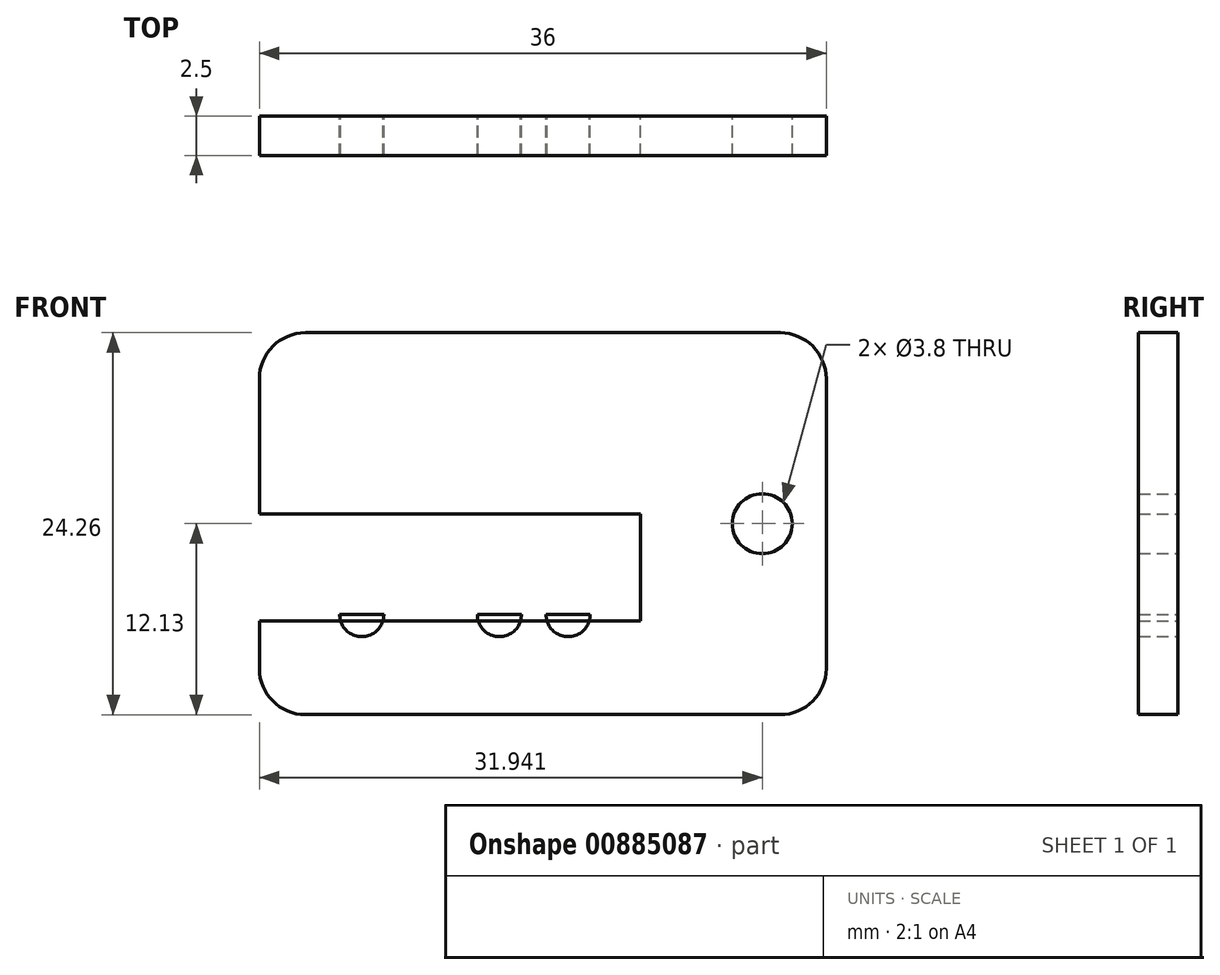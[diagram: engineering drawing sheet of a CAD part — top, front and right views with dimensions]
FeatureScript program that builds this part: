
annotation { "Feature Type Name" : "Feature", "Feature Type Description" : "" }
export const myFeature = defineFeature(function(context is Context, id is Id, definition is map)
    precondition{}
    {
        {
            var Q0;
            Q0=qCreatedBy(makeId("Front.planeOp"),FACE);
            var sketch = newSketch(context, id + "F0", { "sketchPlane" : qUnion([Q0])});
            skArc(sketch, "E0", {"start": v(-105.6, -27.46) * mm, "mid": v(-107.66, -28.32) * mm, "end": v(-108.52, -30.38) * mm});
            skArc(sketch, "E1", {"start": v(-108.52, -48.8) * mm, "mid": v(-107.66, -50.86) * mm, "end": v(-105.6, -51.72) * mm});
            skLineSegment(sketch, "E2", {"start": v(-105.6, -27.46) * mm, "end": v(-72.52, -27.46) * mm});
            skLineSegment(sketch, "E3", {"start": v(-72.52, -51.72) * mm, "end": v(-105.6, -51.72) * mm});
            skLineSegment(sketch, "E4", {"start": v(-108.52, -48.8) * mm, "end": v(-108.52, -30.38) * mm});
            skCircle(sketch, "E5", {"center": v(-99.83, -41.38) * mm, "radius": 1.4 * mm});
            skCircle(sketch, "E6", {"center": v(-95.46, -41.38) * mm, "radius": 1.4 * mm});
            skCircle(sketch, "E7", {"center": v(-91.1, -41.38) * mm, "radius": 1.4 * mm});
            skCircle(sketch, "E8", {"center": v(-86.73, -41.38) * mm, "radius": 1.4 * mm});
            skCircle(sketch, "E9", {"center": v(-102.02, -45.37) * mm, "radius": 1.4 * mm});
            skCircle(sketch, "E10", {"center": v(-97.65, -45.37) * mm, "radius": 1.4 * mm});
            skCircle(sketch, "E11", {"center": v(-93.28, -45.37) * mm, "radius": 1.4 * mm});
            skCircle(sketch, "E12", {"center": v(-88.91, -45.37) * mm, "radius": 1.4 * mm});
            skCircle(sketch, "E13", {"center": v(-76.58, -39.6) * mm, "radius": 1.9 * mm});
            skCircle(sketch, "E14", {"center": v(-76.58, -31.97) * mm, "radius": 1.2 * mm});
            skCircle(sketch, "E15", {"center": v(-76.58, -46.7) * mm, "radius": 1.2 * mm});
            skCircle(sketch, "E16", {"center": v(-76.58, -47.72) * mm, "radius": 1.2 * mm});
            skLineSegment(sketch, "E17", {"start": v(-72.52, -43.22) * mm, "end": v(-72.52, -51.72) * mm});
            skArc(sketch, "E18", {"start": v(-75.44, -51.72) * mm, "mid": v(-73.38, -50.86) * mm, "end": v(-72.52, -48.8) * mm});
            skLineSegment(sketch, "E19", {"start": v(-108.52, -43.52) * mm, "end": v(-74.05, -43.52) * mm});
            skLineSegment(sketch, "E20", {"start": v(-108.52, -43.23) * mm, "end": v(-74.04, -43.23) * mm});
            skLineSegment(sketch, "E21", {"start": v(-72.52, -43.22) * mm, "end": v(-72.52, -27.46) * mm});
            skArc(sketch, "E22", {"start": v(-72.52, -30.38) * mm, "mid": v(-73.38, -28.32) * mm, "end": v(-75.44, -27.46) * mm});
            skLineSegment(sketch, "E23", {"start": v(-110.85, -55.44) * mm, "end": v(-77.56, -55.44) * mm, "construction": true});
            skLineSegment(sketch, "E24.bottom", {"start": v(-103.42, -45.37) * mm, "end": v(-100.62, -45.37) * mm});
            skLineSegment(sketch, "E24.top", {"start": v(-103.42, -43.52) * mm, "end": v(-100.62, -43.52) * mm});
            skLineSegment(sketch, "E24.left", {"start": v(-103.42, -45.37) * mm, "end": v(-103.42, -43.52) * mm});
            skLineSegment(sketch, "E24.right", {"start": v(-100.62, -45.37) * mm, "end": v(-100.62, -43.52) * mm});
            skLineSegment(sketch, "E25.bottom", {"start": v(-99.05, -43.52) * mm, "end": v(-96.25, -43.52) * mm});
            skLineSegment(sketch, "E25.top", {"start": v(-99.05, -45.37) * mm, "end": v(-96.25, -45.37) * mm});
            skLineSegment(sketch, "E25.left", {"start": v(-99.05, -43.52) * mm, "end": v(-99.05, -45.37) * mm});
            skLineSegment(sketch, "E25.right", {"start": v(-96.25, -43.52) * mm, "end": v(-96.25, -45.37) * mm});
            skLineSegment(sketch, "E26.bottom", {"start": v(-94.68, -43.52) * mm, "end": v(-91.88, -43.52) * mm});
            skLineSegment(sketch, "E26.top", {"start": v(-94.68, -45.37) * mm, "end": v(-91.88, -45.37) * mm});
            skLineSegment(sketch, "E26.left", {"start": v(-94.68, -43.52) * mm, "end": v(-94.68, -45.37) * mm});
            skLineSegment(sketch, "E26.right", {"start": v(-91.88, -43.52) * mm, "end": v(-91.88, -45.37) * mm});
            skLineSegment(sketch, "E27.bottom", {"start": v(-90.31, -43.52) * mm, "end": v(-87.51, -43.52) * mm});
            skLineSegment(sketch, "E27.top", {"start": v(-90.31, -45.37) * mm, "end": v(-87.51, -45.37) * mm});
            skLineSegment(sketch, "E27.left", {"start": v(-90.31, -43.52) * mm, "end": v(-90.31, -45.37) * mm});
            skLineSegment(sketch, "E27.right", {"start": v(-87.51, -43.52) * mm, "end": v(-87.51, -45.37) * mm});
            skLineSegment(sketch, "E28.bottom", {"start": v(-101.23, -41.38) * mm, "end": v(-98.43, -41.38) * mm});
            skLineSegment(sketch, "E28.top", {"start": v(-101.23, -43.23) * mm, "end": v(-98.43, -43.23) * mm});
            skLineSegment(sketch, "E28.left", {"start": v(-101.23, -41.38) * mm, "end": v(-101.23, -43.23) * mm});
            skLineSegment(sketch, "E28.right", {"start": v(-98.43, -41.38) * mm, "end": v(-98.43, -43.23) * mm});
            skLineSegment(sketch, "E29.bottom", {"start": v(-96.86, -41.38) * mm, "end": v(-94.06, -41.38) * mm});
            skLineSegment(sketch, "E29.top", {"start": v(-96.86, -43.23) * mm, "end": v(-94.06, -43.23) * mm});
            skLineSegment(sketch, "E29.left", {"start": v(-96.86, -41.38) * mm, "end": v(-96.86, -43.23) * mm});
            skLineSegment(sketch, "E29.right", {"start": v(-94.06, -41.38) * mm, "end": v(-94.06, -43.23) * mm});
            skLineSegment(sketch, "E30.bottom", {"start": v(-92.5, -41.38) * mm, "end": v(-89.7, -41.38) * mm});
            skLineSegment(sketch, "E30.top", {"start": v(-92.5, -43.23) * mm, "end": v(-89.7, -43.23) * mm});
            skLineSegment(sketch, "E30.left", {"start": v(-92.5, -41.38) * mm, "end": v(-92.5, -43.23) * mm});
            skLineSegment(sketch, "E30.right", {"start": v(-89.7, -41.38) * mm, "end": v(-89.7, -43.23) * mm});
            skLineSegment(sketch, "E31.bottom", {"start": v(-88.13, -41.38) * mm, "end": v(-85.33, -41.38) * mm});
            skLineSegment(sketch, "E31.top", {"start": v(-88.13, -43.23) * mm, "end": v(-85.33, -43.23) * mm});
            skLineSegment(sketch, "E31.left", {"start": v(-88.13, -41.38) * mm, "end": v(-88.13, -43.23) * mm});
            skLineSegment(sketch, "E31.right", {"start": v(-85.33, -41.38) * mm, "end": v(-85.33, -43.23) * mm});
            skLineSegment(sketch, "E32.bottom", {"start": v(-108.52, -45.77) * mm, "end": v(-84.33, -45.77) * mm});
            skLineSegment(sketch, "E32.top", {"start": v(-108.52, -38.98) * mm, "end": v(-84.33, -38.98) * mm});
            skLineSegment(sketch, "E32.left", {"start": v(-108.52, -45.77) * mm, "end": v(-108.52, -38.98) * mm});
            skLineSegment(sketch, "E32.right", {"start": v(-84.33, -45.77) * mm, "end": v(-84.33, -38.98) * mm});
            skSolve(sketch);
        }
        {
            var Q0;
            {var subQ1=sQuery(id+"F0.wireOp",EDGE,"E0");Q0=makeQuery(id+"F0.imprint","IMPRINT",FACE,{"disambiguationData":[TD([[makeQuery(id+"F0.imprint","IMPRINT",EDGE,{"derivedFrom":subQ1}),1.0]])]});}
            var Q1;
            Q1=makeQuery(id+"F0.imprint","IMPRINT",FACE,{"disambiguationData":[TD([[makeQuery(id+"F0.imprint","IMPRINT",EDGE,{"derivedFrom":sQuery(id+"F0.wireOp",EDGE,"E14")}),1.0]])]});
            var Q2;
            {var subQ0=sQuery(id+"F0.wireOp",EDGE,"E16");var subQ1=sQuery(id+"F0.wireOp",EDGE,"E15");var subQ2=makeQuery(id+"F0.imprint","INTERSECT",VERTEX,{"disambiguationData":[OD(0.0)],"derivedFrom":[subQ1,subQ0]});Q2=makeQuery(id+"F0.imprint","IMPRINT",FACE,{"disambiguationData":[TD([[makeQuery(id+"F0.imprint","IMPRINT",EDGE,{"disambiguationData":[TD([[subQ2,-1.0]])],"derivedFrom":subQ1}),-1.0]])]});}
            var Q3;
            {var subQ0=sQuery(id+"F0.wireOp",EDGE,"E16");var subQ1=sQuery(id+"F0.wireOp",EDGE,"E15");var subQ2=makeQuery(id+"F0.imprint","INTERSECT",VERTEX,{"disambiguationData":[OD(0.0)],"derivedFrom":[subQ1,subQ0]});Q3=makeQuery(id+"F0.imprint","IMPRINT",FACE,{"disambiguationData":[TD([[makeQuery(id+"F0.imprint","IMPRINT",EDGE,{"disambiguationData":[TD([[subQ2,-1.0]])],"derivedFrom":subQ1}),1.0]])]});}
            var Q4;
            {var subQ0=sQuery(id+"F0.wireOp",EDGE,"E16");var subQ1=sQuery(id+"F0.wireOp",EDGE,"E15");var subQ2=makeQuery(id+"F0.imprint","INTERSECT",VERTEX,{"disambiguationData":[OD(0.0)],"derivedFrom":[subQ1,subQ0]});Q4=makeQuery(id+"F0.imprint","IMPRINT",FACE,{"disambiguationData":[TD([[makeQuery(id+"F0.imprint","IMPRINT",EDGE,{"disambiguationData":[TD([[subQ2,1.0]])],"derivedFrom":subQ1}),1.0]])]});}
            var Q5;
            {var subQ0=sQuery(id+"F0.wireOp",EDGE,"E32.bottom");var subQ1=sQuery(id+"F0.wireOp",EDGE,"E9");var subQ2=makeQuery(id+"F0.imprint","INTERSECT",VERTEX,{"disambiguationData":[OD(0.0)],"derivedFrom":[subQ1,subQ0]});Q5=makeQuery(id+"F0.imprint","IMPRINT",FACE,{"disambiguationData":[TD([[makeQuery(id+"F0.imprint","IMPRINT",EDGE,{"disambiguationData":[TD([[subQ2,-1.0]])],"derivedFrom":subQ1}),1.0]])]});}
            var Q6;
            {var subQ0=sQuery(id+"F0.wireOp",EDGE,"E32.bottom");var subQ1=sQuery(id+"F0.wireOp",EDGE,"E10");var subQ2=makeQuery(id+"F0.imprint","INTERSECT",VERTEX,{"disambiguationData":[OD(0.0)],"derivedFrom":[subQ1,subQ0]});Q6=makeQuery(id+"F0.imprint","IMPRINT",FACE,{"disambiguationData":[TD([[makeQuery(id+"F0.imprint","IMPRINT",EDGE,{"disambiguationData":[TD([[subQ2,-1.0]])],"derivedFrom":subQ1}),1.0]])]});}
            var Q7;
            {var subQ0=sQuery(id+"F0.wireOp",EDGE,"E32.bottom");var subQ1=sQuery(id+"F0.wireOp",EDGE,"E11");var subQ2=makeQuery(id+"F0.imprint","INTERSECT",VERTEX,{"disambiguationData":[OD(0.0)],"derivedFrom":[subQ1,subQ0]});Q7=makeQuery(id+"F0.imprint","IMPRINT",FACE,{"disambiguationData":[TD([[makeQuery(id+"F0.imprint","IMPRINT",EDGE,{"disambiguationData":[TD([[subQ2,-1.0]])],"derivedFrom":subQ1}),1.0]])]});}
            var Q8;
            {var subQ0=sQuery(id+"F0.wireOp",EDGE,"E32.bottom");var subQ1=sQuery(id+"F0.wireOp",EDGE,"E12");var subQ2=makeQuery(id+"F0.imprint","INTERSECT",VERTEX,{"disambiguationData":[OD(0.0)],"derivedFrom":[subQ1,subQ0]});Q8=makeQuery(id+"F0.imprint","IMPRINT",FACE,{"disambiguationData":[TD([[makeQuery(id+"F0.imprint","IMPRINT",EDGE,{"disambiguationData":[TD([[subQ2,-1.0]])],"derivedFrom":subQ1}),1.0]])]});}
            extrude(context, id + "F1", {"entities" : qUnion([Q0, Q1, Q2, Q3, Q4, Q5, Q6, Q7, Q8]), "depth" : 2.5 * mm, "offsetDistance" : 25 * mm});
        }
    });
